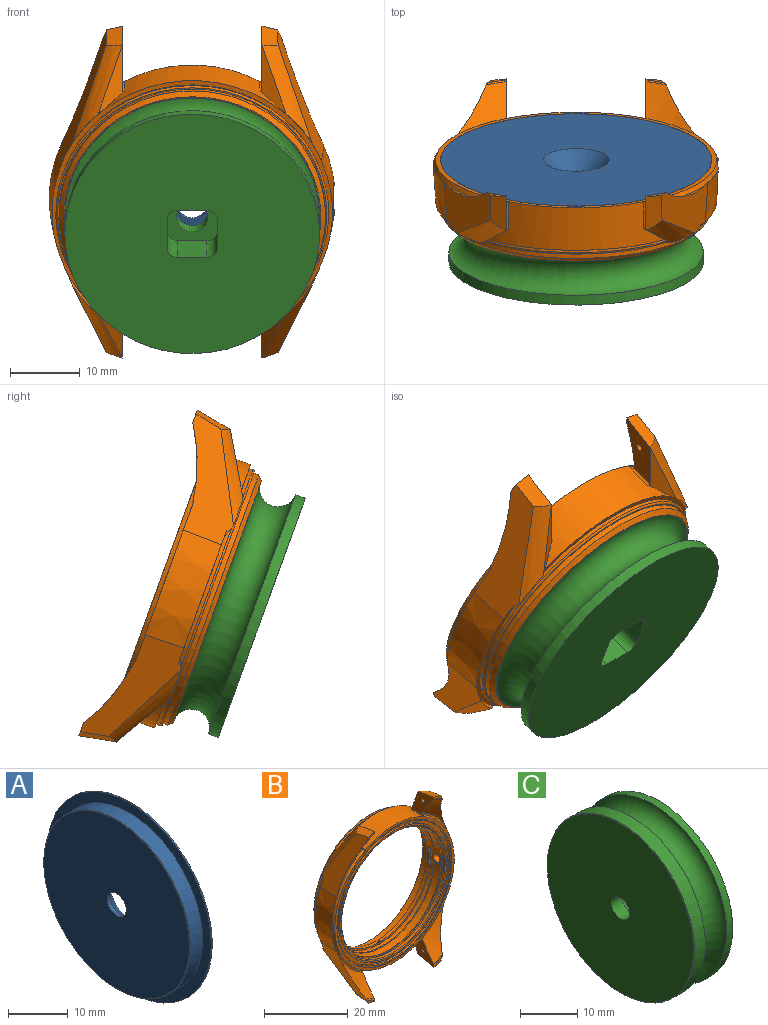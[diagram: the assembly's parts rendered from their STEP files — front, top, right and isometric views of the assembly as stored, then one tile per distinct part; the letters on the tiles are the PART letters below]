
ASSEMBLY  parts=3 mates=2
PART A: 8 faces, bbox 3.3x38.8x38.8 mm
  f0: plane 38.82x38.82mm, normal (1,0,0), area 1112.7mm2, adj f1,f6
  f1: cylinder r=19.41mm len=38.82mm, axis (-1,0,0), area 30.5mm2, adj f0,f2
  f2: plane 38.82x38.82mm, normal (-1,0,0), area 235.7mm2, adj f1,f3
  f3: cylinder r=17.37mm len=34.74mm, axis (-1,0,0), area 316.5mm2, adj f2,f7
  f4: plane 34.54x34.54mm, normal (-1,0,0), area 921.1mm2, adj f5,f7
  f5: cylinder r=2.25mm len=4.5mm, axis (1,0,0), area 10.6mm2, adj f4,f6
  f6: cone r=2.25mm half-angle=45deg, axis (1,0,0), area 77.8mm2, adj f0,f5
  f7: cone r=17.27mm half-angle=45deg, axis (1,0,0), area 15.4mm2, adj f3,f4
PART B: 146 faces, bbox 43.5x13.1x50.1 mm
  f0: plane 36.6x36.6mm, normal (0,1,0), area 168mm2, adj f6,f72,f73,f77,f78,f79,f81,f82
  f1: cylinder r=17.4mm len=34.8mm, axis (0,1,0), area 214mm2, adj f2,f70,f85
  f2: cone r=17.4mm half-angle=45deg, axis (0,-1,0), area 22.5mm2, adj f1,f3,f85
  f3: cylinder r=17.25mm len=34.5mm, axis (0,1,0), area 115.6mm2, adj f2,f5,f71,f80,f84,f85,f86
  f4: cylinder r=1.08mm len=2.82mm, axis (-1,0,0), area 19.2mm2, adj f74,f85
  f5: plane 34.49x16.85mm, normal (0,-1,0), area 26.3mm2, adj f3,f6,f78,f79,f81,f82
  f6: cylinder r=16.75mm len=33.49mm, axis (0,1,0), area 46.6mm2, adj f0,f5,f79,f81
  f7: cone r=20.87mm half-angle=3.8deg, axis (0,-1,0), area 77.2mm2, adj f9,f10,f12,f14,f34,f74,f75,f76
  f8: cone r=20.45mm half-angle=24.8deg, axis (0,1,0), area 29.2mm2, adj f9,f10,f16,f21,f45,f74,f75,f76
  f9: plane 16.44x10.4mm, normal (0,-1,0), area 5.3mm2, adj f7,f8,f14,f21,f51,f75
  f10: plane 16.44x10.4mm, normal (0,-1,0), area 5.3mm2, adj f7,f8,f12,f16,f49,f76
  f11: plane 16.53x10.71mm, normal (-0.92,0.07,0.39), area 87.8mm2, adj f17,f24,f30,f34,f43,f47,f48,f54
  f12: plane 16.53x10.71mm, normal (0.92,0.07,-0.39), area 87.8mm2, adj f7,f10,f23,f31,f34,f42,f49,f53
  f13: plane 16.53x10.71mm, normal (-0.92,0.07,-0.39), area 87.8mm2, adj f17,f22,f32,f34,f41,f47,f50,f52
  f14: plane 16.53x10.71mm, normal (0.92,0.07,0.39), area 87.8mm2, adj f7,f9,f25,f33,f34,f44,f51,f55
  f15: plane 7.95x7.44mm, normal (1,0,0), area 26mm2, adj f24,f26,f46,f47,f48,f54,f59,f90
  f16: plane 7.95x7.44mm, normal (-1,0,0), area 26mm2, adj f8,f10,f23,f27,f49,f53,f57,f87
  f17: cone r=19.87mm half-angle=3.8deg, axis (0,-1,0), area 95.5mm2, adj f11,f13,f34,f47
  f18: plane 7.95x7.44mm, normal (1,0,0), area 26mm2, adj f22,f29,f46,f47,f50,f52,f56,f88
  f19: cylinder r=20.1mm len=25.29mm, axis (0,1,0), area 140.1mm2, adj f27,f29,f34,f45,f87,f88
  f20: cylinder r=20.1mm len=25.29mm, axis (0,1,0), area 140.1mm2, adj f26,f28,f34,f45,f89,f90
  f21: plane 7.95x7.44mm, normal (-1,0,0), area 26mm2, adj f8,f9,f25,f28,f51,f55,f58,f89
  f22: plane 5.69x2.59mm, normal (-0.25,0.18,-0.95), area 11.7mm2, adj f13,f18,f41,f52
  f23: plane 5.69x2.59mm, normal (0.25,0.18,-0.95), area 11.7mm2, adj f12,f16,f42,f53
  f24: plane 5.69x2.59mm, normal (-0.25,0.18,0.95), area 11.7mm2, adj f11,f15,f43,f54
  f25: plane 5.69x2.59mm, normal (0.25,0.18,0.95), area 11.7mm2, adj f14,f21,f44,f55
  f26: plane 8.72x5.19mm, normal (0.47,0.83,0.3), area 13.5mm2, adj f15,f20,f30,f34,f43,f90
  f27: plane 8.72x5.19mm, normal (-0.47,0.83,-0.3), area 13.5mm2, adj f16,f19,f31,f34,f42,f87
  f28: plane 8.72x5.19mm, normal (-0.47,0.83,0.3), area 13.5mm2, adj f20,f21,f33,f34,f44,f89
  f29: plane 8.72x5.19mm, normal (0.47,0.83,-0.3), area 13.5mm2, adj f18,f19,f32,f34,f41,f88
  f30: cone r=20.15mm half-angle=16deg, axis (0,1,0), area 4.9mm2, adj f11,f26,f34,f43
  f31: cone r=20.15mm half-angle=16deg, axis (0,1,0), area 4.9mm2, adj f12,f27,f34,f42
  f32: cone r=20.15mm half-angle=16deg, axis (0,1,0), area 4.9mm2, adj f13,f29,f34,f41
  f33: cone r=20.15mm half-angle=16deg, axis (0,1,0), area 4.9mm2, adj f14,f28,f34,f44
  f34: plane 40.21x40.2mm, normal (0,1,0), area 82.9mm2, adj f7,f11,f12,f13,f14,f17,f19,f20
  f35: plane 36.9x36.9mm, normal (0,1,0), area 17.3mm2, adj f36,f73
  f36: cone r=18.45mm half-angle=45deg, axis (0,-1,0), area 108.4mm2, adj f35,f37
  f37: cylinder r=19.1mm len=38.2mm, axis (0,-1,0), area 90mm2, adj f36,f38
  f38: plane 38.6x38.6mm, normal (0,1,0), area 24.1mm2, adj f37,f39
  f39: torus R=19.3mm, axis (0,-1,0), area 53.4mm2, adj f38,f40
  f40: cone r=19.55mm half-angle=10deg, axis (0,1,0), area 69.2mm2, adj f34,f39
  f41: bspline ~12.87x8.8mm, area 35.7mm2, adj f13,f22,f29,f32
  f42: bspline ~12.87x8.8mm, area 35.7mm2, adj f12,f23,f27,f31
  f43: bspline ~12.87x8.8mm, area 35.7mm2, adj f11,f24,f26,f30
  f44: bspline ~12.87x8.8mm, area 35.7mm2, adj f14,f25,f28,f33
  f45: plane 40.3x40.2mm, normal (0,-1,0), area 85mm2, adj f8,f19,f20,f46,f60,f87,f88,f89
  f46: cone r=20.45mm half-angle=24.8deg, axis (0,1,0), area 30.8mm2, adj f15,f18,f45,f47,f88,f90
  f47: plane 36.7x10.49mm, normal (0,-1,0), area 10.8mm2, adj f11,f13,f15,f17,f18,f46,f48,f50
  f48: torus R=5.72mm, axis (0,1,0), area 35.6mm2, adj f11,f15,f47,f59
  f49: torus R=5.72mm, axis (0,1,0), area 35.6mm2, adj f10,f12,f16,f57
  f50: torus R=5.72mm, axis (0,1,0), area 35.6mm2, adj f13,f18,f47,f56
  f51: torus R=5.72mm, axis (0,1,0), area 35.6mm2, adj f9,f14,f21,f58
  f52: plane 2.7x1.64mm, normal (0,-1,0), area 1.4mm2, adj f13,f18,f22,f56
  f53: plane 2.7x1.64mm, normal (0,-1,0), area 1.4mm2, adj f12,f16,f23,f57
  f54: plane 2.7x1.64mm, normal (0,-1,0), area 1.4mm2, adj f11,f15,f24,f59
  f55: plane 2.7x1.64mm, normal (0,-1,0), area 1.4mm2, adj f14,f21,f25,f58
  f56: torus R=26.45mm, axis (0,-1,0), area 1.2mm2, adj f13,f18,f50,f52
  f57: torus R=26.45mm, axis (0,-1,0), area 1.2mm2, adj f12,f16,f49,f53
  f58: torus R=26.45mm, axis (0,-1,0), area 1.2mm2, adj f14,f21,f51,f55
  f59: torus R=26.45mm, axis (0,-1,0), area 1.2mm2, adj f11,f15,f48,f54
  f60: cylinder r=19.45mm len=38.9mm, axis (0,1,0), area 30.6mm2, adj f45,f61
  f61: plane 38.9x38.9mm, normal (0,-1,0), area 42.4mm2, adj f60,f62
  f62: cylinder r=19.1mm len=38.2mm, axis (0,1,0), area 66mm2, adj f61,f63
  f63: plane 38.2x38.2mm, normal (0,-1,0), area 109.4mm2, adj f62,f64
  f64: cone r=18.17mm half-angle=8deg, axis (0,-1,0), area 69.3mm2, adj f63,f65
  f65: plane 36.5x36.5mm, normal (0,-1,0), area 51mm2, adj f64,f66
  f66: cone r=17.8mm half-angle=60deg, axis (0,-1,0), area 38.4mm2, adj f65,f67
  f67: cylinder r=17.5mm len=35mm, axis (0,1,0), area 93.9mm2, adj f66,f68
  f68: cone r=17.5mm half-angle=60deg, axis (0,1,0), area 38.4mm2, adj f67,f69
  f69: cylinder r=17.8mm len=35.6mm, axis (0,1,0), area 44.7mm2, adj f68,f70
  f70: plane 35.6x35.6mm, normal (0,-1,0), area 44.1mm2, adj f1,f69,f85
  f71: plane 34.49x16.85mm, normal (0,-1,0), area 26.3mm2, adj f3,f72,f77,f78,f82,f83
  f72: cylinder r=16.75mm len=33.49mm, axis (0,1,0), area 46.6mm2, adj f0,f71,f77,f83
  f73: cylinder r=18.3mm len=36.6mm, axis (0,1,0), area 322mm2, adj f0,f35
  f74: plane 5.94x5.04mm, normal (1,0,0), area 16.3mm2, adj f4,f7,f8,f75,f76
  f75: cylinder r=3.23mm len=2.03mm, axis (-1,0,0), area 0.3mm2, adj f7,f8,f9,f74
  f76: cylinder r=3.23mm len=2.03mm, axis (-1,0,0), area 0.3mm2, adj f7,f8,f10,f74
  f77: plane 0.9x0.45mm, normal (1,0,0), area 0.4mm2, adj f0,f71,f72,f78
  f78: cylinder r=0.4mm len=0.9mm, axis (0,1,0), area 1.1mm2, adj f0,f5,f71,f77,f79,f80
  f79: plane 0.9x0.45mm, normal (-1,0,0), area 0.4mm2, adj f0,f5,f6,f78
  f80: plane 0.8x0.35mm, normal (0,1,0), area 0.2mm2, adj f3,f78
  f81: plane 0.9x0.45mm, normal (-1,0,0), area 0.4mm2, adj f0,f5,f6,f82
  f82: cylinder r=0.4mm len=0.9mm, axis (0,1,0), area 1.1mm2, adj f0,f5,f71,f81,f83,f84
  f83: plane 0.9x0.45mm, normal (1,0,0), area 0.4mm2, adj f0,f71,f72,f82
  f84: plane 0.8x0.35mm, normal (0,1,0), area 0.2mm2, adj f3,f82
  f85: cylinder r=5mm len=3.66mm, axis (0,-1,0), area 5.2mm2, adj f1,f2,f3,f4,f70,f86
  f86: plane 3.66x0.35mm, normal (0,-1,0), area 0.6mm2, adj f3,f85
  f87: cylinder r=0.2mm len=4.22mm, axis (0,1,0), area 1.7mm2, adj f8,f16,f19,f27,f45
  f88: cylinder r=0.2mm len=4.22mm, axis (0,1,0), area 1.7mm2, adj f18,f19,f29,f45,f46
  f89: cylinder r=0.2mm len=4.22mm, axis (0,1,0), area 1.7mm2, adj f8,f20,f21,f28,f45
  f90: cylinder r=0.2mm len=4.22mm, axis (0,1,0), area 1.7mm2, adj f15,f20,f26,f45,f46
  f91: cylinder r=0.5mm len=1.52mm, axis (-0.98,0.21,0), area 3.9mm2, adj f15,f92
  f92: cone r=0.5mm half-angle=60deg, axis (0.98,-0.21,0), area 0.9mm2, adj f91
  f93: cylinder r=0.5mm len=1.52mm, axis (0.98,0.21,0), area 3.9mm2, adj f21,f94
  f94: cone r=0.5mm half-angle=60deg, axis (-0.98,-0.21,0), area 0.9mm2, adj f93
  f95: cylinder r=0.5mm len=1.52mm, axis (-0.98,0.21,0), area 3.9mm2, adj f18,f96
  f96: cone r=0.5mm half-angle=60deg, axis (0.98,-0.21,0), area 0.9mm2, adj f95
  f97: cylinder r=0.5mm len=1.52mm, axis (0.98,0.21,0), area 3.9mm2, adj f16,f98
  f98: cone r=0.5mm half-angle=60deg, axis (-0.98,-0.21,0), area 0.9mm2, adj f97
  f99: plane 0.14x0.02mm, normal (-1,0,-0.07), area 0mm2, adj f0,f100,f106,f107
  f100: plane 0.97x0.45mm, normal (0.42,0,-0.91), area 0mm2, adj f0,f99,f101,f107
  f101: plane 0.14x0.02mm, normal (1,0,0.07), area 0mm2, adj f0,f100,f102,f107
  f102: plane 1.02x0.34mm, normal (0.32,0,0.95), area 0mm2, adj f0,f101,f103,f107
  f103: plane 0.15x0.02mm, normal (-1,0,-0.07), area 0mm2, adj f0,f102,f104,f107
  f104: plane 0.31x0.1mm, normal (-0.3,0,-0.95), area 0mm2, adj f0,f103,f105,f107
  f105: plane 0.41x0.03mm, normal (-1,0,-0.07), area 0mm2, adj f0,f104,f106,f107
  f106: plane 0.29x0.13mm, normal (-0.4,0,0.92), area 0mm2, adj f0,f99,f105,f107
  f107: plane 1.03x0.93mm, normal (0,1,0), area 0.3mm2, adj f99,f100,f101,f102,f103,f104,f105,f106
  f108: plane 0.28x0.13mm, normal (-0.41,0,0.91), area 0mm2, adj f107,f109,f112,f113
  f109: cylinder r=1.25mm len=0.19mm, axis (0,-1,0), area 0mm2, adj f107,f108,f110,f113
  f110: cylinder r=2.55mm len=0.21mm, axis (0,-1,0), area 0mm2, adj f107,f109,f111,f113
  f111: plane 0.28x0.09mm, normal (-0.29,0,-0.96), area 0mm2, adj f107,f110,f112,f113
  f112: plane 0.34x0.02mm, normal (1,0,0.07), area 0mm2, adj f107,f108,f111,f113
  f113: plane 0.49x0.34mm, normal (0,1,0), area 0.1mm2, adj f108,f109,f110,f111,f112
  f114: plane 0.36x0.02mm, normal (-1,0,0.06), area 0mm2, adj f0,f115,f120,f121
  f115: plane 0.99x0.06mm, normal (-0.06,0,-1), area 0mm2, adj f0,f114,f116,f121
  f116: plane 0.34x0.02mm, normal (1,0,-0.06), area 0mm2, adj f0,f115,f117,f121
  f117: cylinder r=0.81mm len=0.18mm, axis (0,-1,0), area 0mm2, adj f0,f116,f118,f121
  f118: cylinder r=0.34mm len=0.15mm, axis (0,-1,0), area 0mm2, adj f0,f117,f119,f121
  f119: extruded ~0.4x0.18mm, area 0mm2, adj f0,f118,f120,f121
  f120: extruded ~0.53x0.43mm, area 0mm2, adj f0,f114,f119,f121
  f121: plane 1.02x0.85mm, normal (0,1,0), area 0.4mm2, adj f114,f115,f116,f117,f118,f119,f120,f122
  f122: plane 0.76x0.05mm, normal (0.06,0,1), area 0mm2, adj f121,f123,f128,f145
  f123: plane 0.21x0.02mm, normal (-1,0,0.06), area 0mm2, adj f121,f122,f124,f145
  f124: extruded ~0.17x0.02mm, area 0mm2, adj f121,f123,f125,f145
  f125: extruded ~0.34x0.2mm, area 0mm2, adj f121,f124,f126,f145
  f126: extruded ~0.32x0.08mm, area 0mm2, adj f121,f125,f127,f145
  f127: extruded ~0.24x0.09mm, area 0mm2, adj f121,f126,f128,f145
  f128: plane 0.21x0.02mm, normal (1,0,-0.06), area 0mm2, adj f121,f122,f127,f145
  f129: plane 0.29x0.02mm, normal (-1,0,0), area 0mm2, adj f0,f130,f143,f144
  f130: plane 0.12x0.02mm, normal (0,0,-1), area 0mm2, adj f0,f129,f131,f144
  f131: plane 0.42x0.02mm, normal (1,0,0), area 0mm2, adj f0,f130,f132,f144
  f132: plane 0.37x0.02mm, normal (0,0,1), area 0mm2, adj f0,f131,f133,f144
  f133: extruded ~0.41x0.15mm, area 0mm2, adj f0,f132,f134,f144
  f134: extruded ~0.51x0.51mm, area 0mm2, adj f0,f133,f135,f144
  f135: extruded ~0.52x0.5mm, area 0mm2, adj f0,f134,f136,f144
  f136: extruded ~0.41x0.29mm, area 0mm2, adj f0,f135,f137,f144
  f137: plane 0.12x0.03mm, normal (-0.96,0,0.26), area 0mm2, adj f0,f136,f138,f144
  f138: extruded ~0.29x0.21mm, area 0mm2, adj f0,f137,f139,f144
  f139: extruded ~0.32x0.2mm, area 0mm2, adj f0,f138,f140,f144
  f140: cylinder r=0.52mm len=0.2mm, axis (0,1,0), area 0mm2, adj f0,f139,f141,f144
  f141: extruded ~0.4x0.36mm, area 0mm2, adj f0,f140,f142,f144
  f142: cylinder r=0.47mm len=0.29mm, axis (0,1,0), area 0mm2, adj f0,f141,f143,f144
  f143: plane 0.18x0.02mm, normal (0,0,-1), area 0mm2, adj f0,f129,f142,f144
  f144: plane 1.03x0.92mm, normal (0,1,0), area 0.4mm2, adj f129,f130,f131,f132,f133,f134,f135,f136
  f145: plane 0.77x0.58mm, normal (0,1,0), area 0.4mm2, adj f122,f123,f124,f125,f126,f127,f128
PART C: 16 faces, bbox 9.6x43.6x43.6 mm
  f0: plane 36.5x36.5mm, normal (1,0,0), area 996.4mm2, adj f1,f5,f6,f7,f8,f9,f10,f11
  f1: cylinder r=18.25mm len=36.5mm, axis (-1,0,0), area 172mm2, adj f0,f2
  f2: torus R=18.25mm, axis (-1,0,0), area 867.9mm2, adj f1,f3
  f3: cylinder r=18.25mm len=36.5mm, axis (-1,0,0), area 309.6mm2, adj f2,f15
  f4: plane 36.3x36.3mm, normal (-1,0,0), area 1019mm2, adj f14,f15
  f5: plane 7x4.2mm, normal (0,-1,0), area 29.4mm2, adj f0,f6,f12,f13
  f6: cylinder r=1.5mm len=7mm, axis (1,0,0), area 16.5mm2, adj f0,f5,f7,f13
  f7: plane 7x4.2mm, normal (0,0,-1), area 29.4mm2, adj f0,f6,f8,f13
  f8: cylinder r=1.5mm len=7mm, axis (1,0,0), area 16.5mm2, adj f0,f7,f9,f13
  f9: plane 7x4.2mm, normal (0,1,0), area 29.4mm2, adj f0,f8,f10,f13
  f10: cylinder r=1.5mm len=7mm, axis (1,0,0), area 16.5mm2, adj f0,f9,f11,f13
  f11: plane 7x4.2mm, normal (0,0,1), area 29.4mm2, adj f0,f10,f12,f13
  f12: cylinder r=1.5mm len=7mm, axis (1,0,0), area 16.5mm2, adj f0,f5,f11,f13
  f13: plane 7.2x7.2mm, normal (1,0,0), area 34mm2, adj f5,f6,f7,f8,f9,f10,f11,f12
  f14: cylinder r=2.25mm len=4.5mm, axis (1,0,0), area 36.9mm2, adj f4,f13
  f15: cone r=18.15mm half-angle=45deg, axis (1,0,0), area 16.2mm2, adj f3,f4
PLACE A rot(axis=(-0.5,-0.71,0.5),109.2deg) t=(0,-5.81,16.66)mm
PLACE B rot(axis=(-1,0,0),160deg) t=(0,-2.75,17.77)mm
PLACE C rot(axis=(0.63,-0.44,-0.63),132.1deg) t=(0,-8.31,15.75)mm fixed
MATE planar B.f1 <-> A.f5  axis (0,0.94,0.34) through (0,-2.75,17.77)mm
MATE fastened C.f1 <-> B.f1  axis (0,0.94,0.34) through (0,-9.66,15.26)mm
